# Revit family: DSFM-45-OS-AG_2014
name_source: partatom
category: Specialty Equipment
revit_build: Autodesk Revit 2014 (Build: 20130308_1515(x64)
units: mm (PartAtom-declared; Revit-internal decimal feet)

## types (1)
- 45 OS
    Bumper = Extruded PVC - 747 Chocolate Brown
    Case = Textured Sheet Metal (Steel Painted) - 149 White Satin Matte
    Case Interior - Back Panel = Mirror
    Case Interior - Side Panel = Mirror
    Case Weight = 0.00 lbf
    Close Off Panel = Textured Sheet Metal (Steel Painted) - 701 Black
    Cutsheet URL = http://www.hussmann.com
    Depth = 42 1/2"
    Description = Medium Depth Service Merchandiser for Fresh Seafood Applications
    Door Frame = Plastic - 144 Mist Gray
    End Weight = 0.00 lbf
    Glazing = Glass
    Height = 52 1/4"
    Manufacturer = Hussmann Corporation
    Manufacturer Disclaimer = The information in this file is not intended to be an exact representation of the corresponding Hussmann product.  Further, we reserve the right to change or revise specifications and product design in connection with any feature of our products. Such changes do not entitle the buyer to corresponding changes, improvements, additions, or replacements for equipment previously sold or shipped.
    Model = DSFM - 45 Outside Wedge with Angled Glass
    Model URL = http://www.hussmann.com
    Note from Manufacturer = This model only comes in one size.
    Number of Supports = 2
    Refrig. Liquid = Liquid
    Refrig. Suction = Suction
    Refrigeration Lines Liquid = 3/8"
    Refrigeration Lines Suction = 5/8"
    Revit Family Date = 09/20/2016
    Shelves = Sheet Metal (Steel Painted) - 701 Black
    Splashguard = Stainless Steel
    Total Weight = 0.00 lbf
    Trim = Stainless Steel
    Type Comments = Chino
    URL = www.hussmann.com
    Waste Drain = 1 1/2"
    Width = 65 3/4"

## geometry (parser evidence)
native form markers: Sweep x5
no freeform markers — native parametric forms only
